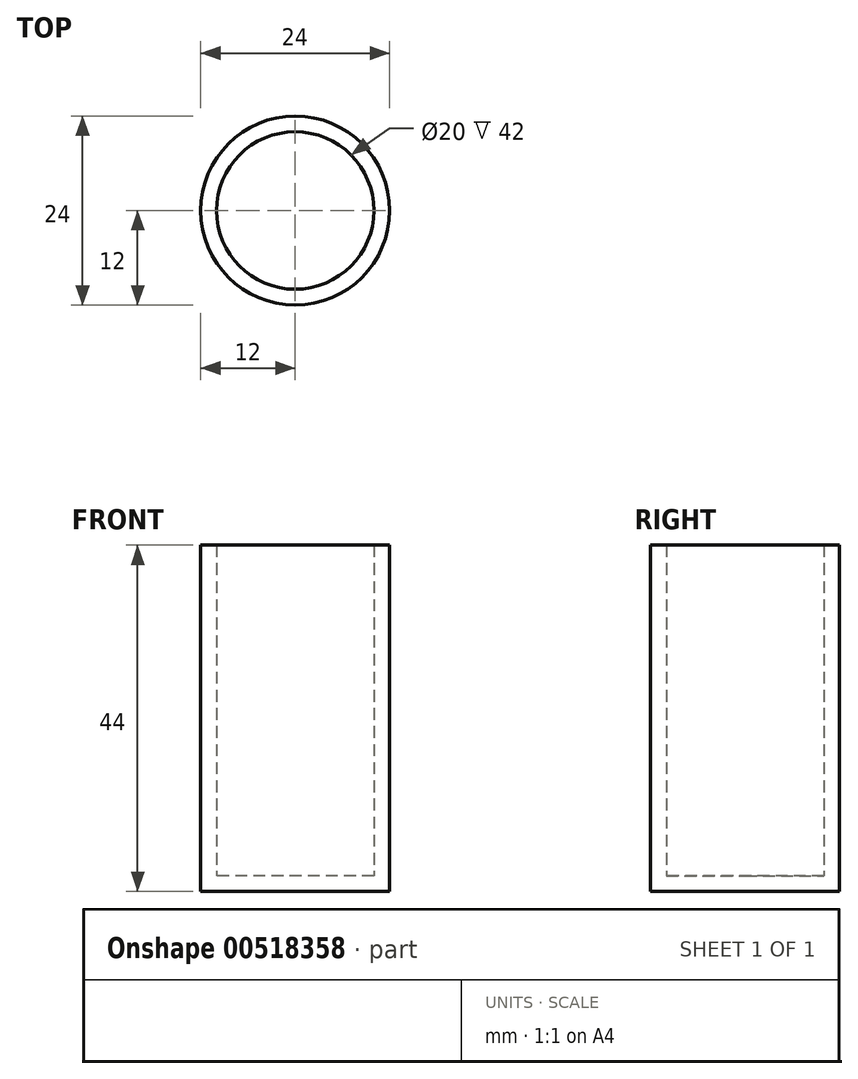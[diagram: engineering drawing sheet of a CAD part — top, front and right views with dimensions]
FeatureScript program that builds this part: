
annotation { "Feature Type Name" : "Feature", "Feature Type Description" : "" }
export const myFeature = defineFeature(function(context is Context, id is Id, definition is map)
    precondition{}
    {
        {
            var Q0;
            Q0=qCreatedBy(makeId("Top.planeOp"),FACE);
            var sketch = newSketch(context, id + "F0", { "sketchPlane" : qUnion([Q0])});
            skCircle(sketch, "E0", {"center": v(0, 0) * mm, "radius": 12 * mm});
            skSolve(sketch);
        }
        {
            var Q0;
            Q0 = qSketchRegion(id + "F0", true);
            extrude(context, id + "F1", {"entities" : qUnion([Q0]), "depth" : 2 * mm, "offsetDistance" : 25 * mm});
        }
        {
            var Q0;
            Q0=makeQuery(id+"F1.opExtrude","CAP_FACE",FACE,{"disambiguationData":[OSD([sQuery(id+"F0.wireOp",EDGE,"E0")])],"isStart":false});
            var sketch = newSketch(context, id + "F2", { "sketchPlane" : qUnion([Q0])});
            skCircle(sketch, "E1", {"center": v(0, 0) * mm, "radius": 10 * mm});
            skCircle(sketch, "E2", {"center": v(0, 0) * mm, "radius": 12 * mm});
            skSolve(sketch);
        }
        {
            var Q0;
            Q0 = qSketchRegion(id + "F2", true);
            extrude(context, id + "F3", {"entities" : qUnion([Q0]), "operationType" : NewBodyOperationType.ADD, "depth" : 42 * mm, "offsetDistance" : 25 * mm});
        }
    });
